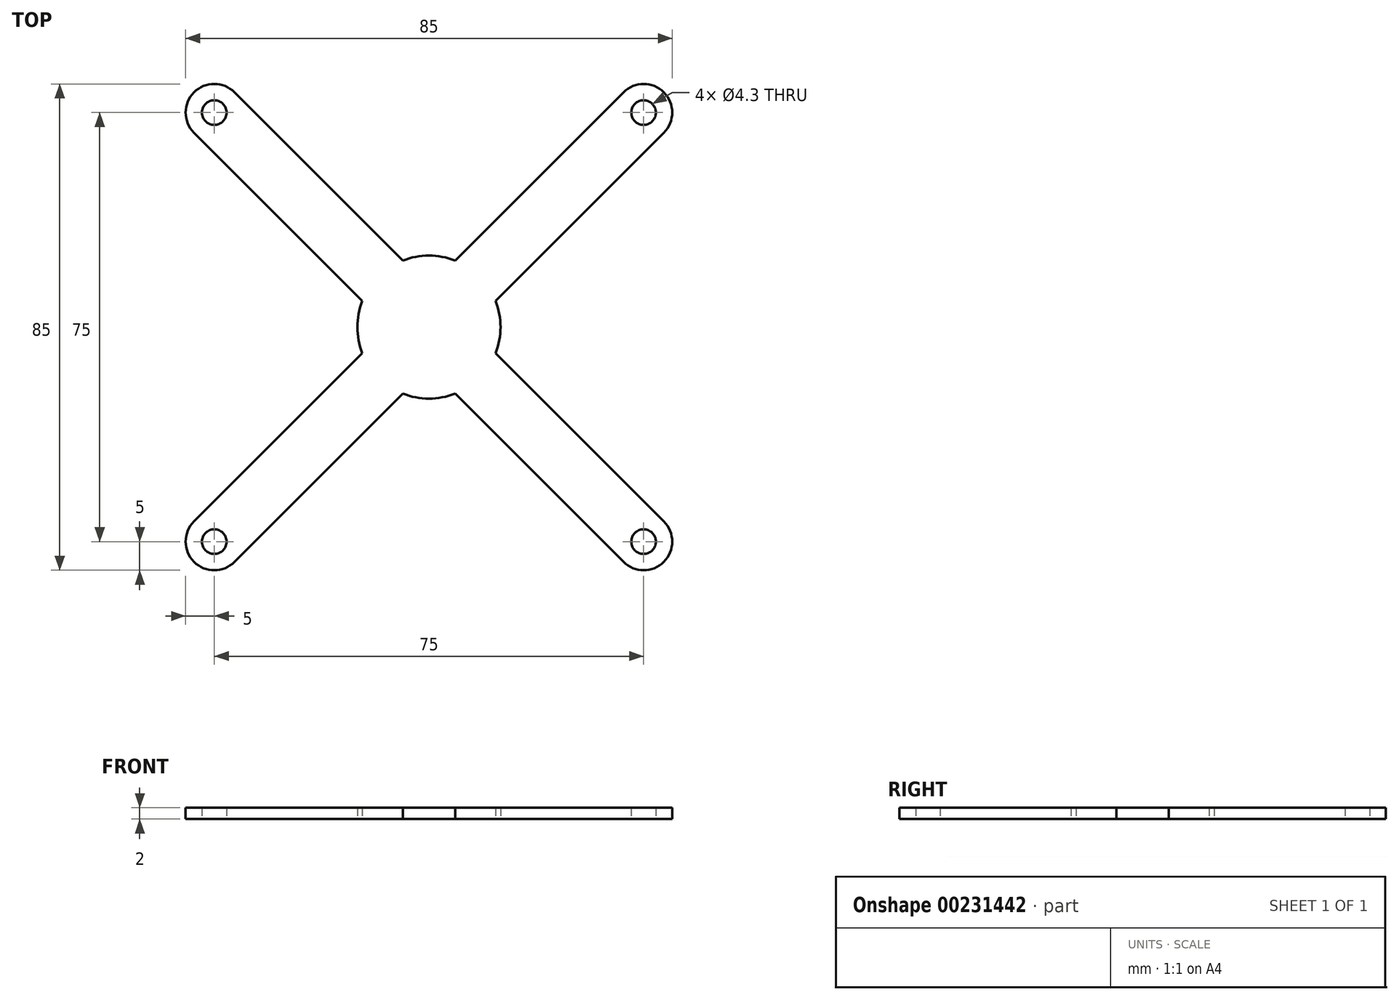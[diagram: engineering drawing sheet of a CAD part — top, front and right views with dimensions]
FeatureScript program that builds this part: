
annotation { "Feature Type Name" : "Feature", "Feature Type Description" : "" }
export const myFeature = defineFeature(function(context is Context, id is Id, definition is map)
    precondition{}
    {
        {
            var Q0;
            Q0=qCreatedBy(makeId("Top.planeOp"),FACE);
            var sketch = newSketch(context, id + "F0", { "sketchPlane" : qUnion([Q0])});
            skLineSegment(sketch, "E0.bottom", {"start": v(-37.5, 37.5) * mm, "end": v(37.5, 37.5) * mm, "construction": true});
            skLineSegment(sketch, "E0.top", {"start": v(-37.5, -37.5) * mm, "end": v(37.5, -37.5) * mm, "construction": true});
            skLineSegment(sketch, "E0.left", {"start": v(-37.5, 37.5) * mm, "end": v(-37.5, -37.5) * mm, "construction": true});
            skLineSegment(sketch, "E0.right", {"start": v(37.5, 37.5) * mm, "end": v(37.5, -37.5) * mm, "construction": true});
            skPoint(sketch, "E0.middle", {"position": v(0, 0) * mm});
            skCircle(sketch, "E1", {"center": v(-37.5, 37.5) * mm, "radius": 2.15 * mm});
            skCircle(sketch, "E2", {"center": v(37.5, 37.5) * mm, "radius": 2.15 * mm});
            skCircle(sketch, "E3", {"center": v(37.5, -37.5) * mm, "radius": 2.15 * mm});
            skCircle(sketch, "E4", {"center": v(-37.5, -37.5) * mm, "radius": 2.15 * mm});
            skArc(sketch, "E5", {"start": v(-33.96, 41.04) * mm, "mid": v(-41.04, 41.04) * mm, "end": v(-41.04, 33.96) * mm});
            skArc(sketch, "E6", {"start": v(41.04, 33.96) * mm, "mid": v(41.04, 41.04) * mm, "end": v(33.96, 41.04) * mm});
            skArc(sketch, "E7", {"start": v(-41.04, -33.96) * mm, "mid": v(-41.04, -41.04) * mm, "end": v(-33.96, -41.04) * mm});
            skArc(sketch, "E8", {"start": v(33.96, -41.04) * mm, "mid": v(41.04, -41.04) * mm, "end": v(41.04, -33.96) * mm});
            skLineSegment(sketch, "E9", {"start": v(-33.96, 41.04) * mm, "end": v(-4.57, 11.64) * mm});
            skLineSegment(sketch, "E10", {"start": v(-41.04, 33.96) * mm, "end": v(-11.64, 4.57) * mm});
            skLineSegment(sketch, "E11", {"start": v(41.04, 33.96) * mm, "end": v(11.64, 4.57) * mm});
            skLineSegment(sketch, "E12", {"start": v(33.96, 41.04) * mm, "end": v(4.57, 11.64) * mm});
            skArc(sketch, "E13", {"start": v(-11.64, 4.57) * mm, "mid": v(-12.5, 0) * mm, "end": v(-11.64, -4.57) * mm});
            skLineSegment(sketch, "E14", {"start": v(-41.04, -33.96) * mm, "end": v(-11.64, -4.57) * mm});
            skLineSegment(sketch, "E15", {"start": v(-33.96, -41.04) * mm, "end": v(-4.57, -11.64) * mm});
            skLineSegment(sketch, "E16", {"start": v(41.04, -33.96) * mm, "end": v(11.64, -4.57) * mm});
            skLineSegment(sketch, "E17", {"start": v(33.96, -41.04) * mm, "end": v(4.57, -11.64) * mm});
            skArc(sketch, "E18.trimOffspring", {"start": v(-4.57, -11.64) * mm, "mid": v(0, -12.5) * mm, "end": v(4.57, -11.64) * mm});
            skArc(sketch, "E19.trimOffspring", {"start": v(11.64, -4.57) * mm, "mid": v(12.5, 0) * mm, "end": v(11.64, 4.57) * mm});
            skArc(sketch, "E20.trimOffspring", {"start": v(4.57, 11.64) * mm, "mid": v(0, 12.5) * mm, "end": v(-4.57, 11.64) * mm});
            skSolve(sketch);
        }
        {
            var Q0;
            Q0=makeQuery(id+"F0.imprint","IMPRINT",FACE,{"disambiguationData":[TD([[makeQuery(id+"F0.imprint","IMPRINT",EDGE,{"derivedFrom":sQuery(id+"F0.wireOp",EDGE,"E1")}),-1.0]])]});
            extrude(context, id + "F1", {"entities" : qUnion([Q0]), "depth" : 2 * mm});
        }
    });
